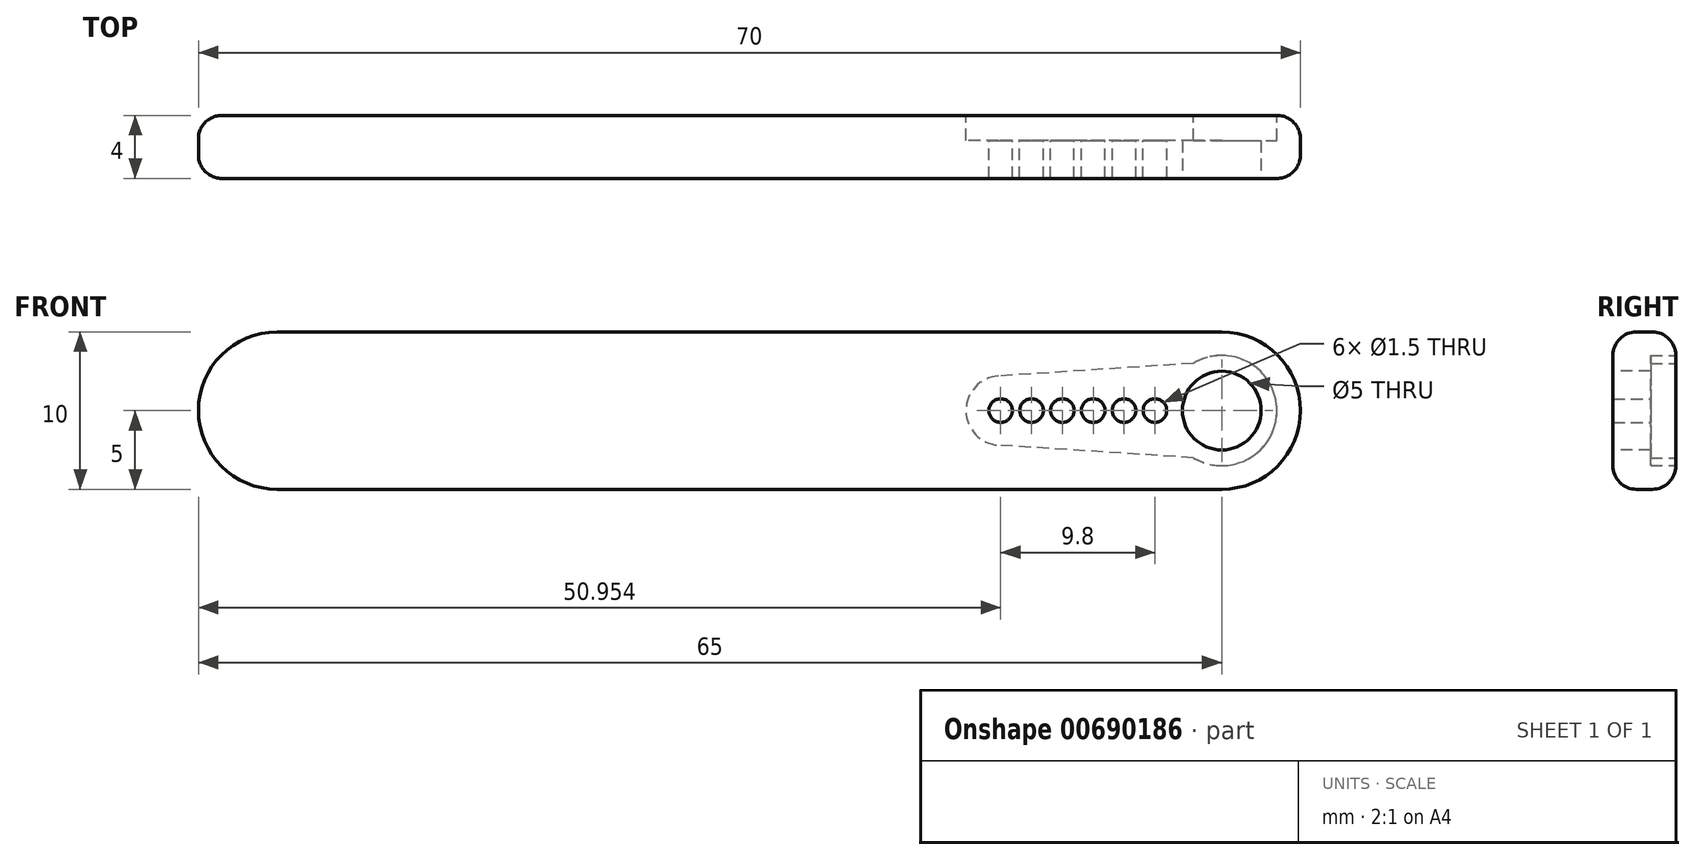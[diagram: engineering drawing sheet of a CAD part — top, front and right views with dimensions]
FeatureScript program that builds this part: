
annotation { "Feature Type Name" : "Feature", "Feature Type Description" : "" }
export const myFeature = defineFeature(function(context is Context, id is Id, definition is map)
    precondition{}
    {
        {
            var Q0;
            Q0=qCreatedBy(makeId("Front.planeOp"),FACE);
            var sketch = newSketch(context, id + "F0", { "sketchPlane" : qUnion([Q0])});
            skLineSegment(sketch, "E0.bottom", {"start": v(0, 5) * mm, "end": v(70, 5) * mm});
            skLineSegment(sketch, "E0.top", {"start": v(0, -5) * mm, "end": v(70, -5) * mm});
            skLineSegment(sketch, "E0.left", {"start": v(0, 5) * mm, "end": v(0, -5) * mm});
            skLineSegment(sketch, "E0.right", {"start": v(70, 5) * mm, "end": v(70, -5) * mm});
            skPoint(sketch, "E0.middle", {"position": v(35, 0) * mm});
            skCircle(sketch, "E1", {"center": v(65, 0) * mm, "radius": 2.5 * mm});
            skSolve(sketch);
        }
        {
            var Q0;
            Q0=makeQuery(id+"F0.imprint","IMPRINT",FACE,{"disambiguationData":[TD([[makeQuery(id+"F0.imprint","IMPRINT",EDGE,{"derivedFrom":sQuery(id+"F0.wireOp",EDGE,"E0.bottom")}),-1.0]])]});
            extrude(context, id + "F1", {"entities" : qUnion([Q0]), "oppositeDirection" : true, "depth" : 4 * mm, "offsetDistance" : 25 * mm});
        }
        {
            var Q0;
            {var subQ1=sQuery(id+"FelzQ8irgmPJCEx_0.wireOp",EDGE,"nqU3fDqP-7IzM-8UvB-soxe-GbgdAJMVhA7a");var subQ3=sQuery(id+"FelzQ8irgmPJCEx_0.wireOp",EDGE,"Wf30qy7B-L3EY-ubdY-4ofm-RBPNTBmtIuBS");var subQ4=sQuery(id+"FelzQ8irgmPJCEx_0.wireOp",EDGE,"0P1yvjZw-iLbS-eAF6-OBv0-oRI93wy17Ioi");var subQ5=sQuery(id+"FelzQ8irgmPJCEx_0.wireOp",EDGE,"IxcgXgfj-hqSl-lfnA-CyWF-p1c6ZB3lQplE");var subQ6=sQuery(id+"FelzQ8irgmPJCEx_0.wireOp",EDGE,"m4ObQz0p-uqgI-Xgwy-2KGq-14yM282HVRsK");var subQ11=makeQuery(id+"FwwyKOTNBZ8lxIx_1.opExtrude","SWEPT_FACE",FACE,{"disambiguationData":[OSD([sQuery(id+"FWpOroBoYfux5cT_1.wireOp",EDGE,"6cmiH4eE-dqzF-GbjJ-dGX1-cgJiLYN27mcO.top")])]});Q0=makeQuery(id+"F1.boolean.opBoolean","MERGE",FACE,{"derivedFrom":[makeQuery(id+"F8gD7zZAfkwsQIA_2.opBoolean","SPLIT",FACE,{"disambiguationData":[TD([makeQuery(id+"FFOvh7GgsPYjLSs_0.opExtrude","CAP_FACE",FACE,{"disambiguationData":[OSD([subQ6,subQ5,subQ4,subQ3,subQ1])],"isStart":true})])],"derivedFrom":subQ11}),makeQuery(id+"F8gD7zZAfkwsQIA_2.opBoolean","SPLIT",FACE,{"disambiguationData":[TD([makeQuery(id+"FwCsV6hsPOMot3H_1.1.FFOvh7GgsPYjLSs_0.opExtrude","CAP_FACE",FACE,{"disambiguationData":[OSD([subQ6,subQ5,subQ4,subQ3,subQ1])],"isStart":true})])],"derivedFrom":subQ11}),makeQuery(id+"F1.opExtrude","CAP_FACE",FACE,{"disambiguationData":[OSD([sQuery(id+"F0.wireOp",EDGE,"E0.bottom"),sQuery(id+"F0.wireOp",EDGE,"E0.top"),sQuery(id+"F0.wireOp",EDGE,"E0.left"),sQuery(id+"F0.wireOp",EDGE,"E0.right"),sQuery(id+"F0.wireOp",EDGE,"E1")])],"isStart":false})]});}
            var sketch = newSketch(context, id + "F2", { "sketchPlane" : qUnion([Q0])});
            skArc(sketch, "E2", {"start": v(-63.2, 3) * mm, "mid": v(-68.5, 0) * mm, "end": v(-63.2, -3) * mm});
            skLineSegment(sketch, "E3", {"start": v(-65, 3.5) * mm, "end": v(-65, -3.5) * mm, "construction": true});
            skLineSegment(sketch, "E4", {"start": v(-63.2, 3) * mm, "end": v(-50.81, 2.2) * mm});
            skLineSegment(sketch, "E5.MirrorCS", {"start": v(-63.2, -3) * mm, "end": v(-50.81, -2.2) * mm});
            skArc(sketch, "E6", {"start": v(-50.81, -2.2) * mm, "mid": v(-48.75, 0) * mm, "end": v(-50.81, 2.2) * mm});
            skSolve(sketch);
        }
        {
            var Q0;
            Q0=qSketchRegion(id+"F2",true);
            extrude(context, id + "F3", {"entities" : qUnion([Q0]), "operationType" : NewBodyOperationType.REMOVE, "oppositeDirection" : true, "depth" : 1.6 * mm, "offsetDistance" : 25 * mm});
        }
        {
            var Q0;
            Q0=makeQuery(id+"F1.opExtrude","SWEPT_EDGE",EDGE,{"disambiguationData":[OSD([sQuery(id+"F0.wireOp",EDGE,"E0.bottom"),sQuery(id+"F0.wireOp",EDGE,"E0.right")])]});
            var Q1;
            Q1=makeQuery(id+"F1.opExtrude","SWEPT_EDGE",EDGE,{"disambiguationData":[OSD([sQuery(id+"F0.wireOp",EDGE,"E0.top"),sQuery(id+"F0.wireOp",EDGE,"E0.right")])]});
            var Q2;
            Q2=makeQuery(id+"F1.opExtrude","SWEPT_EDGE",EDGE,{"disambiguationData":[OSD([sQuery(id+"F0.wireOp",EDGE,"E0.bottom"),sQuery(id+"F0.wireOp",EDGE,"E0.left")])]});
            var Q3;
            Q3=makeQuery(id+"F1.opExtrude","SWEPT_EDGE",EDGE,{"disambiguationData":[OSD([sQuery(id+"F0.wireOp",EDGE,"E0.top"),sQuery(id+"F0.wireOp",EDGE,"E0.left")])]});
            fillet(context, id + "F4", {"entities" : qUnion([Q0, Q1, Q2, Q3]), "radius" : 5 * mm, "tangentPropagation" : true, "allowEdgeOverflow" : false});
        }
        {
            var Q0;
            Q0=makeQuery(id+"F3.boolean.opBoolean","COPY",FACE,{"derivedFrom":makeQuery(id+"F3.opExtrude","CAP_FACE",FACE,{"disambiguationData":[OSD([sQuery(id+"F2.wireOp",EDGE,"E2"),sQuery(id+"F2.wireOp",EDGE,"E4"),sQuery(id+"F2.wireOp",EDGE,"E5.MirrorCS"),sQuery(id+"F2.wireOp",EDGE,"4e372829-45e8-4768-ac35-bef2567a82a80.MirrorCS"),sQuery(id+"F2.wireOp",EDGE,"84e0c534-16ce-4d88-b8c0-036f2b0803bb0.MirrorCS"),sQuery(id+"F2.wireOp",EDGE,"E6"),sQuery(id+"F2.wireOp",EDGE,"d8f68f25-7c4b-45c6-9a1e-f2330f06db270.MirrorCS"),sQuery(id+"F2.wireOp",EDGE,"d5227d3a-9a23-44e3-9c63-5c1f9854272e.trimOffspring")])],"isStart":false})});
            var sketch = newSketch(context, id + "F5", { "sketchPlane" : qUnion([Q0])});
            skCircle(sketch, "E7", {"center": v(-50.95, 0) * mm, "radius": 0.75 * mm});
            skCircle(sketch, "E8.1.0.0", {"center": v(-52.91, 0) * mm, "radius": 0.75 * mm});
            skCircle(sketch, "E8.2.0.0", {"center": v(-54.87, 0) * mm, "radius": 0.75 * mm});
            skCircle(sketch, "E8.3.0.0", {"center": v(-56.83, 0) * mm, "radius": 0.75 * mm});
            skCircle(sketch, "E8.4.0.0", {"center": v(-58.8, 0) * mm, "radius": 0.75 * mm});
            skCircle(sketch, "E8.5.0.0", {"center": v(-60.75, 0) * mm, "radius": 0.75 * mm});
            skLineSegment(sketch, "E8.direction1", {"start": v(-52.91, 0) * mm, "end": v(-50.95, 0) * mm, "construction": true});
            skSolve(sketch);
        }
        {
            var Q0;
            Q0=qSketchRegion(id+"F5",true);
            extrude(context, id + "F6", {"entities" : qUnion([Q0]), "operationType" : NewBodyOperationType.REMOVE, "endBound" : BoundingType.UP_TO_NEXT, "oppositeDirection" : true, "depth" : 25 * mm, "offsetDistance" : 25 * mm});
        }
        {
            var Q0;
            Q0=makeQuery(id+"F1.opExtrude","CAP_EDGE",EDGE,{"disambiguationData":[OSD([sQuery(id+"F0.wireOp",EDGE,"E0.bottom")])],"isStart":false});
            var Q1;
            Q1=makeQuery(id+"F1.opExtrude","CAP_EDGE",EDGE,{"disambiguationData":[OSD([sQuery(id+"F0.wireOp",EDGE,"E0.bottom")])],"isStart":true});
            fillet(context, id + "F7", {"entities" : qUnion([Q0, Q1]), "radius" : 1.5 * mm, "tangentPropagation" : true, "allowEdgeOverflow" : false});
        }
        {
            var Q0;
            Q0=qCreatedBy(makeId("Right.planeOp"),FACE);
            cPlane(context, id + "F8", {"entities" : qUnion([Q0]), "cplaneType" : CPlaneType.OFFSET, "offset" : 47 * mm, "width" : 150 * mm, "height" : 150 * mm});
        }
    });
